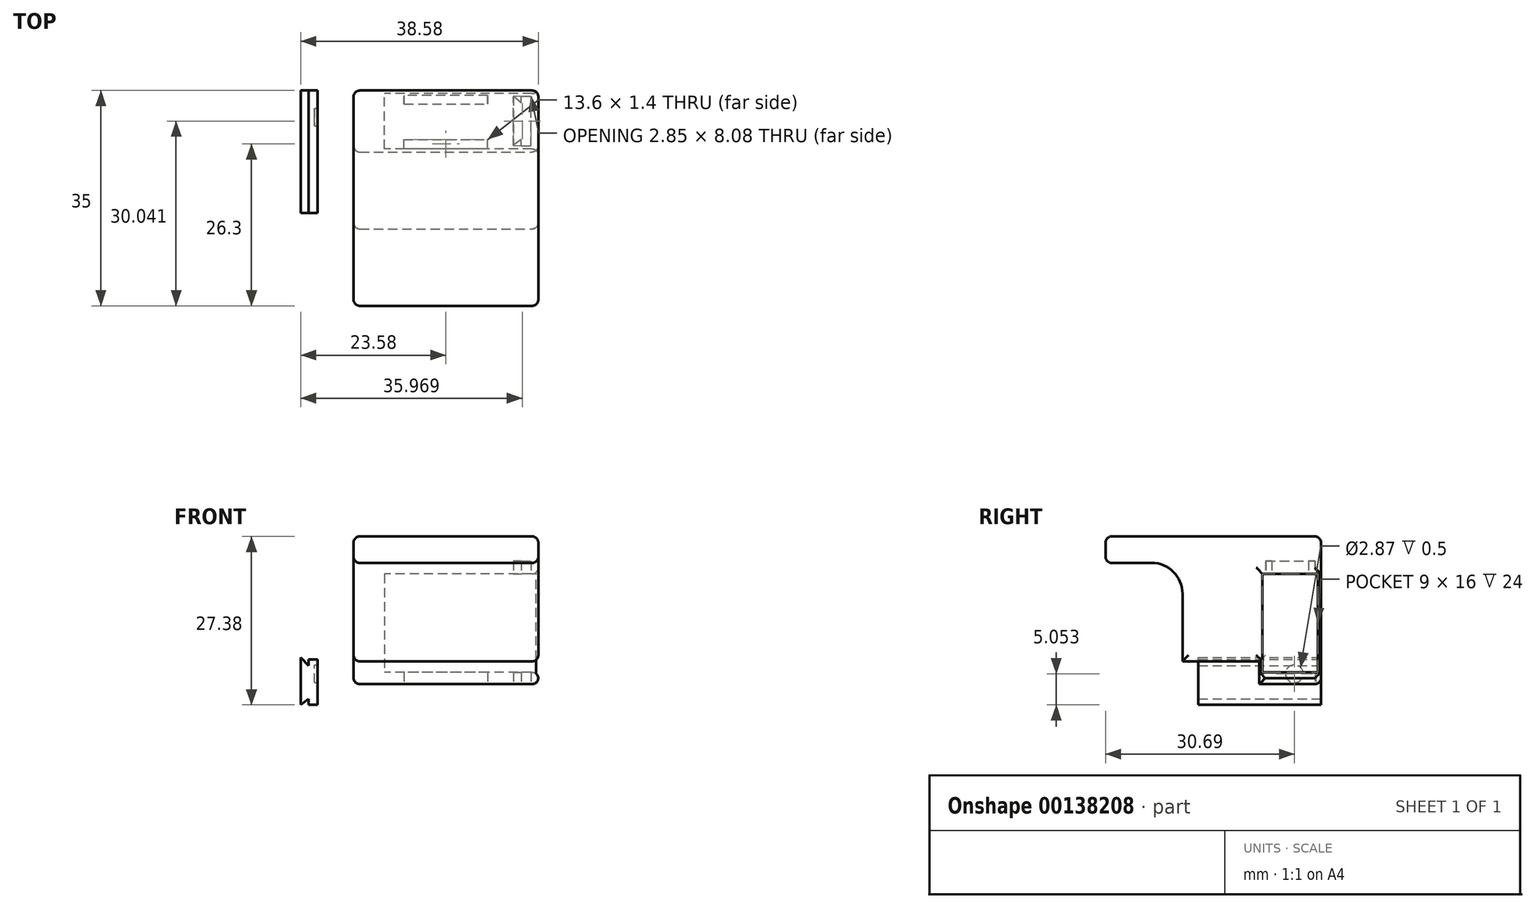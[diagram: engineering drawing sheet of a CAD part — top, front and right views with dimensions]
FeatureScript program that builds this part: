
annotation { "Feature Type Name" : "Feature", "Feature Type Description" : "" }
export const myFeature = defineFeature(function(context is Context, id is Id, definition is map)
    precondition{}
    {
        {
            var Q0;
            Q0=qCreatedBy(makeId("Front.planeOp"),FACE);
            var sketch = newSketch(context, id + "F0", { "sketchPlane" : qUnion([Q0])});
            skLineSegment(sketch, "E0", {"start": v(0, 24) * mm, "end": v(-15, 24) * mm});
            skLineSegment(sketch, "E1", {"start": v(-15, 24) * mm, "end": v(-15, 0) * mm});
            skLineSegment(sketch, "E2", {"start": v(-15, 0) * mm, "end": v(0, 0) * mm});
            skLineSegment(sketch, "E3.MirrorCS", {"start": v(15, 0) * mm, "end": v(0, 0) * mm});
            skLineSegment(sketch, "E4.MirrorCS", {"start": v(0, 24) * mm, "end": v(15, 24) * mm});
            skLineSegment(sketch, "E5.MirrorCS", {"start": v(15, 24) * mm, "end": v(15, 0) * mm});
            skSolve(sketch);
        }
        {
            var Q0;
            Q0 = qSketchRegion(id + "F0", true);
            extrude(context, id + "F1", {"entities" : qUnion([Q0]), "depth" : 35 * mm});
        }
        {
            var Q0;
            Q0=makeQuery(id+"F1.opExtrude","SWEPT_FACE",FACE,{"disambiguationData":[OSD([sQuery(id+"F0.wireOp",EDGE,"E5.MirrorCS")])]});
            var sketch = newSketch(context, id + "F2", { "sketchPlane" : qUnion([Q0])});
            skLineSegment(sketch, "E6", {"start": v(-35, 3.7) * mm, "end": v(-10, 3.7) * mm});
            skLineSegment(sketch, "E7", {"start": v(-10, 3.7) * mm, "end": v(-10, 0) * mm});
            skLineSegment(sketch, "E8", {"start": v(-10, 0) * mm, "end": v(-35, 0) * mm});
            skLineSegment(sketch, "E9", {"start": v(-35, 0) * mm, "end": v(-35, 3.7) * mm});
            skSolve(sketch);
        }
        {
            var Q0;
            Q0 = qSketchRegion(id + "F2", true);
            extrude(context, id + "F3", {"entities" : qUnion([Q0]), "operationType" : NewBodyOperationType.REMOVE, "oppositeDirection" : true, "depth" : 40 * mm});
        }
        {
            var Q0;
            Q0=makeQuery(id+"F1.opExtrude","SWEPT_FACE",FACE,{"disambiguationData":[OSD([sQuery(id+"F0.wireOp",EDGE,"E5.MirrorCS")])]});
            var sketch = newSketch(context, id + "F4", { "sketchPlane" : qUnion([Q0])});
            skLineSegment(sketch, "E10", {"start": v(-35, 3.7) * mm, "end": v(-35, 19.7) * mm});
            skLineSegment(sketch, "E11", {"start": v(-35, 19.7) * mm, "end": v(-27.5, 19.7) * mm});
            skLineSegment(sketch, "E12", {"start": v(-22.5, 14.7) * mm, "end": v(-22.5, 3.7) * mm});
            skPoint(sketch, "E13.visualSharp", {"position": v(-22.5, 19.7) * mm});
            skArc(sketch, "E13.filletArc", {"start": v(-22.5, 14.7) * mm, "mid": v(-23.96, 18.24) * mm, "end": v(-27.5, 19.7) * mm});
            skSolve(sketch);
        }
        {
            var Q0;
            {var subQ1=sQuery(id+"F4.wireOp",EDGE,"E10");Q0=makeQuery(id+"F4.imprint","IMPRINT",FACE,{"disambiguationData":[TD([[makeQuery(id+"F4.imprint","IMPRINT",EDGE,{"derivedFrom":subQ1}),1.0]])]});}
            extrude(context, id + "F5", {"entities" : qUnion([Q0]), "operationType" : NewBodyOperationType.REMOVE, "oppositeDirection" : true, "depth" : 35 * mm});
        }
        {
            var Q0;
            Q0=qCreatedBy(makeId("Right.planeOp"),FACE);
            var sketch = newSketch(context, id + "F6", { "sketchPlane" : qUnion([Q0])});
            skLineSegment(sketch, "E14", {"start": v(-2.97, 0.01) * mm, "end": v(-2.97, 0.01) * mm});
            skLineSegment(sketch, "E15.bottom", {"start": v(-9.5, 17.92) * mm, "end": v(-0.5, 17.92) * mm});
            skLineSegment(sketch, "E15.top", {"start": v(-9.5, 1.92) * mm, "end": v(-0.5, 1.92) * mm});
            skLineSegment(sketch, "E15.left", {"start": v(-9.5, 17.92) * mm, "end": v(-9.5, 1.92) * mm});
            skLineSegment(sketch, "E15.right", {"start": v(-0.5, 17.92) * mm, "end": v(-0.5, 1.92) * mm});
            skSolve(sketch);
        }
        {
            var Q0;
            Q0 = qSketchRegion(id + "F6", true);
            var Q1;
            Q1 = qSketchRegion(id + "F9", true);
            extrude(context, id + "F7", {"entities" : qUnion([Q0, Q1]), "operationType" : NewBodyOperationType.REMOVE, "endBound" : BoundingType.UP_TO_NEXT, "depth" : 10 * mm});
        }
        {
            var Q0;
            Q0 = qSketchRegion(id + "F6", true);
            extrude(context, id + "F8", {"entities" : qUnion([Q0]), "operationType" : NewBodyOperationType.REMOVE, "oppositeDirection" : true, "depth" : 10 * mm});
        }
        {
            var Q0;
            Q0=qCreatedBy(makeId("Top.planeOp"),FACE);
            var sketch = newSketch(context, id + "F9", { "sketchPlane" : qUnion([Q0])});
            skLineSegment(sketch, "E16.bottom", {"start": v(-6.8, -9.4) * mm, "end": v(6.8, -9.4) * mm});
            skLineSegment(sketch, "E16.top", {"start": v(-6.8, -8) * mm, "end": v(6.8, -8) * mm});
            skLineSegment(sketch, "E16.left", {"start": v(-6.8, -9.4) * mm, "end": v(-6.8, -8) * mm});
            skLineSegment(sketch, "E16.right", {"start": v(6.8, -9.4) * mm, "end": v(6.8, -8) * mm});
            skSolve(sketch);
        }
        {
            var Q0;
            Q0 = qSketchRegion(id + "F9", true);
            extrude(context, id + "F10", {"entities" : qUnion([Q0]), "operationType" : NewBodyOperationType.REMOVE, "depth" : 3 * mm});
        }
        {
            var Q0;
            Q0=makeQuery(id+"F1.opExtrude","SWEPT_FACE",FACE,{"disambiguationData":[OSD([sQuery(id+"F0.wireOp",EDGE,"E2"),sQuery(id+"F0.wireOp",EDGE,"E3.MirrorCS")])]});
            var sketch = newSketch(context, id + "F11", { "sketchPlane" : qUnion([Q0])});
            skLineSegment(sketch, "E17.bottom", {"start": v(-6.8, 2.2) * mm, "end": v(6.8, 2.2) * mm});
            skLineSegment(sketch, "E17.top", {"start": v(-6.8, 0.8) * mm, "end": v(6.8, 0.8) * mm});
            skLineSegment(sketch, "E17.left", {"start": v(-6.8, 2.2) * mm, "end": v(-6.8, 0.8) * mm});
            skLineSegment(sketch, "E17.right", {"start": v(6.8, 2.2) * mm, "end": v(6.8, 0.8) * mm});
            skSolve(sketch);
        }
        {
            var Q0;
            Q0=makeQuery(id+"F11.imprint","IMPRINT",FACE,{"disambiguationData":[TD([[makeQuery(id+"F11.imprint","IMPRINT",EDGE,{"derivedFrom":sQuery(id+"F11.wireOp",EDGE,"E17.bottom")}),-1.0]])]});
            extrude(context, id + "F12", {"entities" : qUnion([Q0]), "operationType" : NewBodyOperationType.REMOVE, "oppositeDirection" : true, "depth" : 4 * mm});
        }
        {
            var Q0;
            Q0=makeQuery(id+"F1.opExtrude","SWEPT_FACE",FACE,{"disambiguationData":[OSD([sQuery(id+"F0.wireOp",EDGE,"E2"),sQuery(id+"F0.wireOp",EDGE,"E3.MirrorCS")])]});
            var sketch = newSketch(context, id + "F13", { "sketchPlane" : qUnion([Q0])});
            skLineSegment(sketch, "E18.bottom", {"start": v(12.21, 9) * mm, "end": v(13.81, 9) * mm});
            skLineSegment(sketch, "E18.top", {"start": v(12.21, 1) * mm, "end": v(13.81, 1) * mm});
            skLineSegment(sketch, "E18.left", {"start": v(12.21, 9) * mm, "end": v(12.21, 1) * mm});
            skLineSegment(sketch, "E18.right", {"start": v(13.81, 9) * mm, "end": v(13.81, 1) * mm});
            skLineSegment(sketch, "E19", {"start": v(12.21, 8) * mm, "end": v(10.96, 8.92) * mm});
            skLineSegment(sketch, "E20", {"start": v(10.96, 8.92) * mm, "end": v(10.96, 0.92) * mm});
            skLineSegment(sketch, "E21", {"start": v(10.96, 0.92) * mm, "end": v(12.21, 2) * mm});
            skSolve(sketch);
        }
        {
            var Q0;
            Q0 = qSketchRegion(id + "F13", true);
            extrude(context, id + "F14", {"entities" : qUnion([Q0]), "operationType" : NewBodyOperationType.REMOVE, "oppositeDirection" : true, "depth" : 20 * mm});
        }
        {
            var Q0;
            Q0=qCreatedBy(makeId("Front.planeOp"),FACE);
            var sketch = newSketch(context, id + "F15", { "sketchPlane" : qUnion([Q0])});
            skLineSegment(sketch, "E22.bottom", {"start": v(-22.33, 4.02) * mm, "end": v(-20.83, 4.02) * mm});
            skLineSegment(sketch, "E22.top", {"start": v(-22.33, -3.38) * mm, "end": v(-20.83, -3.38) * mm});
            skLineSegment(sketch, "E22.left", {"start": v(-22.33, 4.02) * mm, "end": v(-22.33, -3.38) * mm});
            skLineSegment(sketch, "E22.right", {"start": v(-20.83, 4.02) * mm, "end": v(-20.83, -3.38) * mm});
            skLineSegment(sketch, "E23", {"start": v(-22.33, 3.02) * mm, "end": v(-23.58, 4.33) * mm});
            skLineSegment(sketch, "E24", {"start": v(-23.58, 4.33) * mm, "end": v(-23.58, -3.37) * mm});
            skLineSegment(sketch, "E25", {"start": v(-23.58, -3.37) * mm, "end": v(-22.33, -2.38) * mm});
            skSolve(sketch);
        }
        {
            var Q0;
            Q0=makeQuery(id+"F1.opExtrude","SWEPT_FACE",FACE,{"disambiguationData":[OSD([sQuery(id+"F0.wireOp",EDGE,"E1")])]});
            fillet(context, id + "F16", {"entities" : qUnion([Q0]), "radius" : 1 * mm, "tangentPropagation" : true, "allowEdgeOverflow" : false});
        }
        {
            var Q0;
            {var subQ0=sQuery(id+"F15.wireOp",EDGE,"E23");Q0=makeQuery(id+"F15.imprint","IMPRINT",FACE,{"disambiguationData":[TD([[makeQuery(id+"F15.imprint","IMPRINT",EDGE,{"derivedFrom":subQ0}),1.0]])]});}
            var Q1;
            {var subQ3=sQuery(id+"F15.wireOp",EDGE,"E22.bottom");Q1=makeQuery(id+"F15.imprint","IMPRINT",FACE,{"disambiguationData":[TD([[makeQuery(id+"F15.imprint","IMPRINT",EDGE,{"derivedFrom":subQ3}),-1.0]])]});}
            extrude(context, id + "F17", {"entities" : qUnion([Q0, Q1]), "depth" : 19.9 * mm});
        }
        {
            var Q0;
            Q0=makeQuery(id+"F1.opExtrude","SWEPT_FACE",FACE,{"disambiguationData":[OSD([sQuery(id+"F0.wireOp",EDGE,"E5.MirrorCS")])]});
            fillet(context, id + "F18", {"entities" : qUnion([Q0]), "radius" : 1 * mm, "tangentPropagation" : true, "allowEdgeOverflow" : false});
        }
        {
            var Q0;
            Q0=makeQuery(id+"F1.opExtrude","CAP_FACE",FACE,{"disambiguationData":[OSD([sQuery(id+"F0.wireOp",EDGE,"E0"),sQuery(id+"F0.wireOp",EDGE,"E1"),sQuery(id+"F0.wireOp",EDGE,"E2"),sQuery(id+"F0.wireOp",EDGE,"E3.MirrorCS"),sQuery(id+"F0.wireOp",EDGE,"E4.MirrorCS"),sQuery(id+"F0.wireOp",EDGE,"E5.MirrorCS")])],"isStart":true});
            fillet(context, id + "F19", {"entities" : qUnion([Q0]), "radius" : 1 * mm, "tangentPropagation" : true, "allowEdgeOverflow" : false});
        }
        {
            var Q0;
            Q0=makeQuery(id+"F1.opExtrude","CAP_FACE",FACE,{"disambiguationData":[OSD([sQuery(id+"F0.wireOp",EDGE,"E0"),sQuery(id+"F0.wireOp",EDGE,"E1"),sQuery(id+"F0.wireOp",EDGE,"E2"),sQuery(id+"F0.wireOp",EDGE,"E3.MirrorCS"),sQuery(id+"F0.wireOp",EDGE,"E4.MirrorCS"),sQuery(id+"F0.wireOp",EDGE,"E5.MirrorCS")])],"isStart":false});
            fillet(context, id + "F20", {"entities" : qUnion([Q0]), "radius" : 1 * mm, "tangentPropagation" : true, "allowEdgeOverflow" : false});
        }
        {
            var Q0;
            Q0=makeQuery(id+"F17.opExtrude","SWEPT_FACE",FACE,{"disambiguationData":[OSD([sQuery(id+"F15.wireOp",EDGE,"E22.right")])]});
            var sketch = newSketch(context, id + "F21", { "sketchPlane" : qUnion([Q0])});
            skCircle(sketch, "E26", {"center": v(-4.31, 1.67) * mm, "radius": 1.43 * mm});
            skSolve(sketch);
        }
        {
            var Q0;
            Q0 = qSketchRegion(id + "F21", true);
            extrude(context, id + "F22", {"entities" : qUnion([Q0]), "operationType" : NewBodyOperationType.REMOVE, "oppositeDirection" : true, "depth" : 0.5 * mm});
        }
    });
